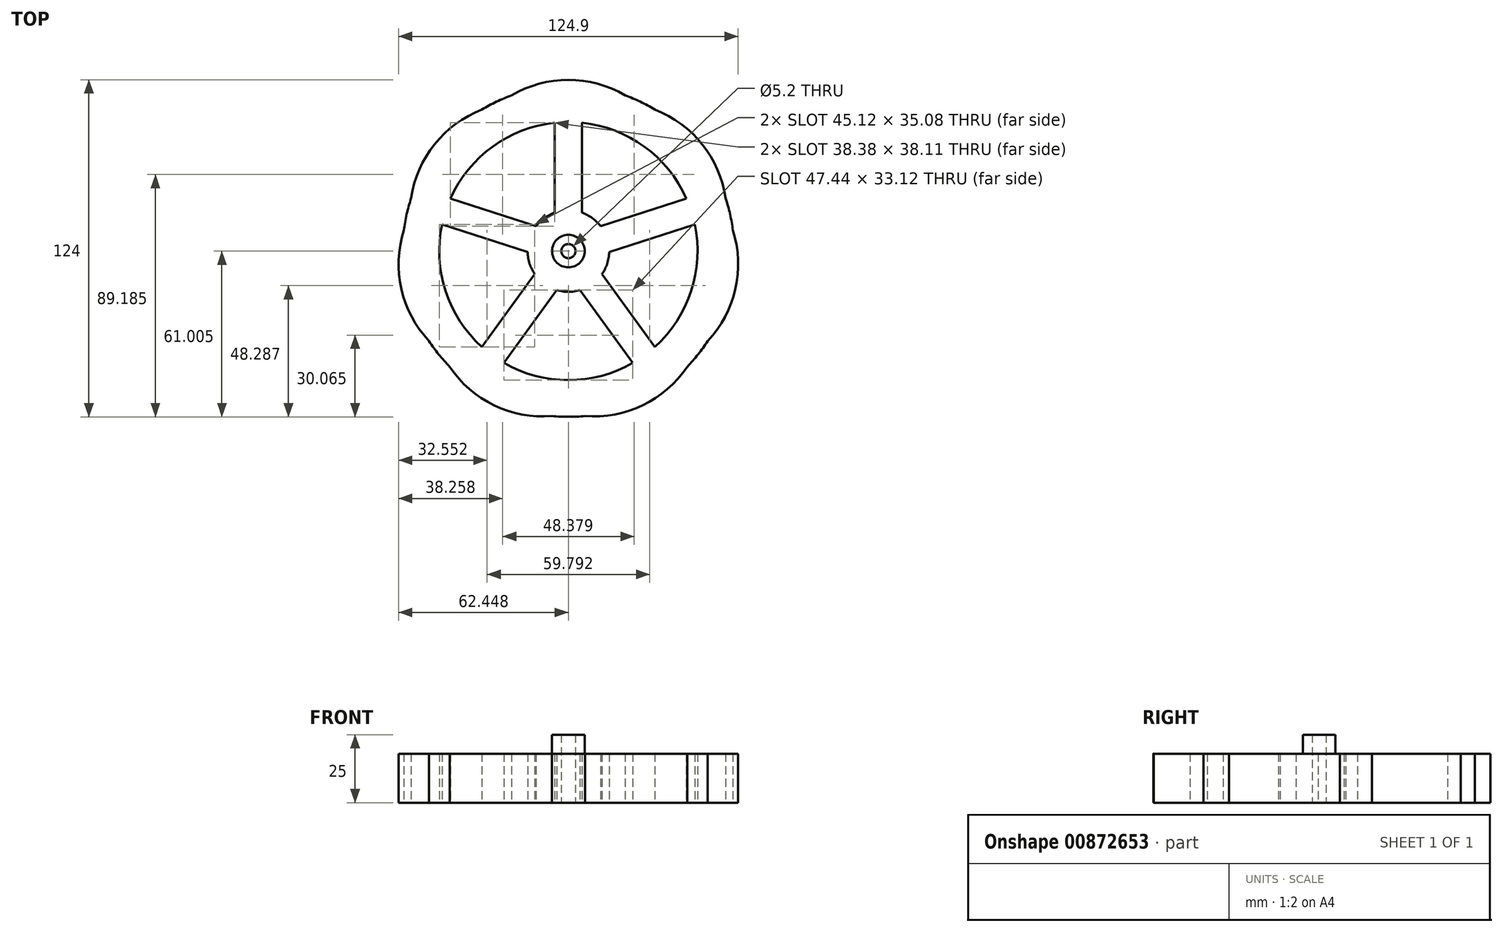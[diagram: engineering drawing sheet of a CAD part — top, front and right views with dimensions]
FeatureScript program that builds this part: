
annotation { "Feature Type Name" : "Feature", "Feature Type Description" : "" }
export const myFeature = defineFeature(function(context is Context, id is Id, definition is map)
    precondition{}
    {
        {
            var Q0;
            Q0=qCreatedBy(makeId("Top.planeOp"),FACE);
            var sketch = newSketch(context, id + "F0", { "sketchPlane" : qUnion([Q0])});
            skCircle(sketch, "E0", {"center": v(-2.92, 4.13) * mm, "radius": 63 * mm, "construction": true});
            skArc(sketch, "E1", {"start": v(-60.75, 23.56) * mm, "mid": v(-62.4, 17.7) * mm, "end": v(-63.45, 11.72) * mm});
            skLineSegment(sketch, "E2", {"start": v(-2.92, 4.13) * mm, "end": v(-2.92, 67.13) * mm, "construction": true});
            skLineSegment(sketch, "E3", {"start": v(-2.92, 4.13) * mm, "end": v(-24.47, 63.34) * mm, "construction": true});
            skLineSegment(sketch, "E4", {"start": v(-2.92, 4.13) * mm, "end": v(18.62, 63.34) * mm, "construction": true});
            skArc(sketch, "E5", {"start": v(17.94, 61.46) * mm, "mid": v(-2.92, 67.13) * mm, "end": v(-23.79, 61.46) * mm});
            skArc(sketch, "E6", {"start": v(-7.92, 51.37) * mm, "mid": v(-30.84, 42.56) * mm, "end": v(-46.3, 23.49) * mm});
            skArc(sketch, "E7", {"start": v(-17.92, 3.75) * mm, "mid": v(-17.19, -0.5) * mm, "end": v(-15.28, -4.37) * mm});
            skLineSegment(sketch, "E8.0", {"start": v(2.08, 18.28) * mm, "end": v(2.08, 51.37) * mm});
            skLineSegment(sketch, "E9.0", {"start": v(-7.92, 18.28) * mm, "end": v(-7.92, 51.37) * mm});
            skLineSegment(sketch, "E10.1.0", {"start": v(-17.92, 3.75) * mm, "end": v(-49.4, 13.98) * mm});
            skLineSegment(sketch, "E10.1.1", {"start": v(-14.83, 13.26) * mm, "end": v(-46.3, 23.49) * mm});
            skLineSegment(sketch, "E10.2.0", {"start": v(-7.19, -10.25) * mm, "end": v(-26.64, -37.02) * mm});
            skLineSegment(sketch, "E10.2.1", {"start": v(-15.28, -4.37) * mm, "end": v(-34.73, -31.14) * mm});
            skLineSegment(sketch, "E11.1.3.0", {"start": v(9.44, -4.37) * mm, "end": v(28.89, -31.14) * mm});
            skLineSegment(sketch, "E11.3.3.0", {"start": v(1.35, -10.25) * mm, "end": v(20.8, -37.02) * mm});
            skLineSegment(sketch, "E11.1.4.0", {"start": v(8.98, 13.26) * mm, "end": v(40.46, 23.49) * mm});
            skLineSegment(sketch, "E11.3.4.0", {"start": v(12.07, 3.75) * mm, "end": v(43.55, 13.98) * mm});
            skArc(sketch, "E12.trimOffspring", {"start": v(40.46, 23.49) * mm, "mid": v(25, 42.56) * mm, "end": v(2.08, 51.37) * mm});
            skArc(sketch, "E13.trimOffspring", {"start": v(28.89, -31.14) * mm, "mid": v(42.25, -10.54) * mm, "end": v(43.55, 13.98) * mm});
            skArc(sketch, "E14.trimOffspring", {"start": v(-26.64, -37.02) * mm, "mid": v(-2.92, -43.37) * mm, "end": v(20.8, -37.02) * mm});
            skArc(sketch, "E15.trimOffspring", {"start": v(-49.4, 13.98) * mm, "mid": v(-48.1, -10.54) * mm, "end": v(-34.73, -31.14) * mm});
            skArc(sketch, "E16.trimOffspring", {"start": v(-7.19, -10.25) * mm, "mid": v(-2.92, -10.87) * mm, "end": v(1.35, -10.25) * mm});
            skArc(sketch, "E17.trimOffspring", {"start": v(9.44, -4.37) * mm, "mid": v(11.34, -0.5) * mm, "end": v(12.07, 3.75) * mm});
            skArc(sketch, "E18.trimOffspring", {"start": v(8.98, 13.26) * mm, "mid": v(5.9, 16.27) * mm, "end": v(2.08, 18.28) * mm});
            skArc(sketch, "E19.trimOffspring", {"start": v(-7.92, 18.28) * mm, "mid": v(-11.74, 16.27) * mm, "end": v(-14.83, 13.26) * mm});
            skArc(sketch, "E20.1.0", {"start": v(-34.73, 56.19) * mm, "mid": v(-52.18, 43.41) * mm, "end": v(-60.75, 23.56) * mm});
            skArc(sketch, "E20.2.0", {"start": v(-63.45, 11.72) * mm, "mid": v(-64.34, -9.88) * mm, "end": v(-54.16, -28.96) * mm});
            skArc(sketch, "E20.3.0", {"start": v(-46.6, -38.46) * mm, "mid": v(-30.26, -52.63) * mm, "end": v(-9, -56.56) * mm});
            skArc(sketch, "E20.4.0", {"start": v(3.15, -56.56) * mm, "mid": v(24.41, -52.63) * mm, "end": v(40.75, -38.46) * mm});
            skArc(sketch, "E20.5.0", {"start": v(48.32, -28.96) * mm, "mid": v(58.5, -9.88) * mm, "end": v(57.6, 11.72) * mm});
            skArc(sketch, "E21.1.6.0", {"start": v(54.9, 23.56) * mm, "mid": v(46.33, 43.41) * mm, "end": v(28.89, 56.19) * mm});
            skArc(sketch, "E22.trimOffspring", {"start": v(-23.79, 61.46) * mm, "mid": v(-29.39, 59.1) * mm, "end": v(-34.73, 56.19) * mm});
            skArc(sketch, "E23.trimOffspring", {"start": v(-54.16, -28.96) * mm, "mid": v(-50.61, -33.9) * mm, "end": v(-46.6, -38.46) * mm});
            skArc(sketch, "E24.trimOffspring", {"start": v(-9, -56.56) * mm, "mid": v(-2.92, -56.87) * mm, "end": v(3.15, -56.56) * mm});
            skArc(sketch, "E25.trimOffspring", {"start": v(40.75, -38.46) * mm, "mid": v(44.77, -33.9) * mm, "end": v(48.32, -28.96) * mm});
            skArc(sketch, "E26.trimOffspring", {"start": v(57.6, 11.72) * mm, "mid": v(56.55, 17.7) * mm, "end": v(54.9, 23.56) * mm});
            skArc(sketch, "E27.trimOffspring", {"start": v(28.89, 56.19) * mm, "mid": v(23.54, 59.1) * mm, "end": v(17.94, 61.46) * mm});
            skCircle(sketch, "E28", {"center": v(-2.92, 4.13) * mm, "radius": 2.6 * mm});
            skCircle(sketch, "E29", {"center": v(-2.92, 4.13) * mm, "radius": 6 * mm});
            skSolve(sketch);
        }
        {
            var Q0;
            Q0=makeQuery(id+"F0.imprint","IMPRINT",FACE,{"disambiguationData":[TD([[makeQuery(id+"F0.imprint","IMPRINT",EDGE,{"derivedFrom":sQuery(id+"F0.wireOp",EDGE,"E28")}),-1.0]])]});
            extrude(context, id + "F1", {"entities" : qUnion([Q0]), "depth" : 25 * mm, "offsetDistance" : 25 * mm});
        }
        {
            var Q0;
            Q0=makeQuery(id+"F0.imprint","IMPRINT",FACE,{"disambiguationData":[TD([[makeQuery(id+"F0.imprint","IMPRINT",EDGE,{"derivedFrom":sQuery(id+"F0.wireOp",EDGE,"E1")}),1.0]])]});
            extrude(context, id + "F2", {"entities" : qUnion([Q0]), "operationType" : NewBodyOperationType.ADD, "depth" : 18 * mm, "offsetDistance" : 25 * mm});
        }
    });
